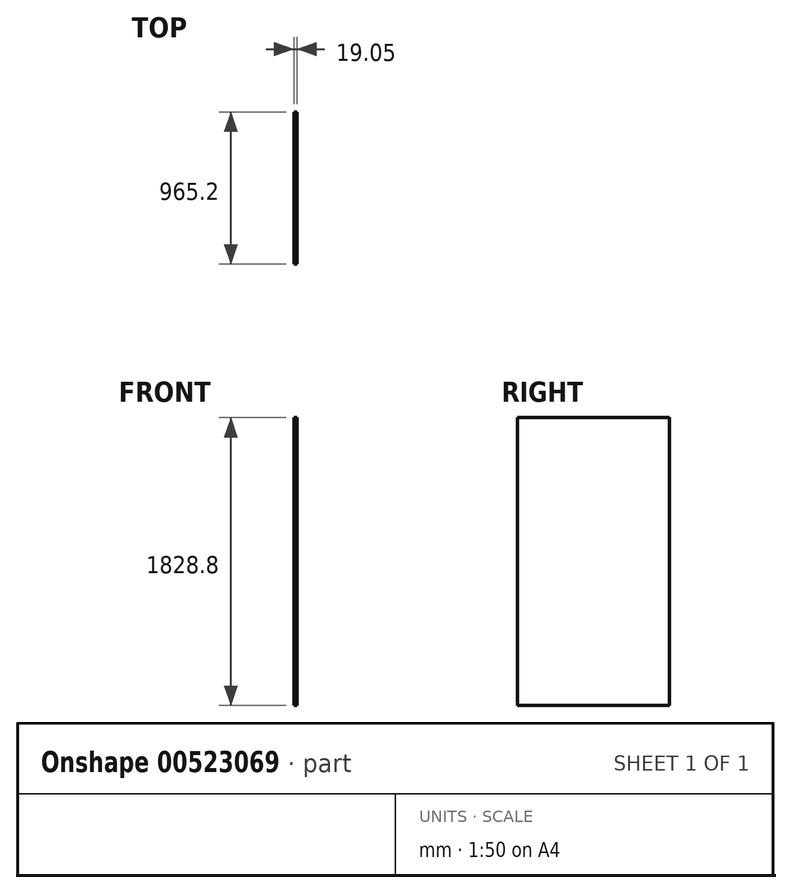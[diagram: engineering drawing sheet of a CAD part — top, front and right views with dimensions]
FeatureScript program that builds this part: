
annotation { "Feature Type Name" : "Feature", "Feature Type Description" : "" }
export const myFeature = defineFeature(function(context is Context, id is Id, definition is map)
    precondition{}
    {
        {
            var Q0;
            Q0=qCreatedBy(makeId("Right.planeOp"),FACE);
            var sketch = newSketch(context, id + "F0", { "sketchPlane" : qUnion([Q0])});
            skLineSegment(sketch, "E0.bottom", {"start": v(0, 0) * mm, "end": v(965.2, 0) * mm});
            skLineSegment(sketch, "E0.top", {"start": v(0, 1828.8) * mm, "end": v(965.2, 1828.8) * mm});
            skLineSegment(sketch, "E0.left", {"start": v(0, 0) * mm, "end": v(0, 1828.8) * mm});
            skLineSegment(sketch, "E0.right", {"start": v(965.2, 0) * mm, "end": v(965.2, 1828.8) * mm});
            skSolve(sketch);
        }
        {
            var Q0;
            Q0=qSketchRegion(id+"F0",true);
            extrude(context, id + "F1", {"entities" : qUnion([Q0]), "depth" : 19.05 * mm, "offsetDistance" : 25.4 * mm});
        }
    });
